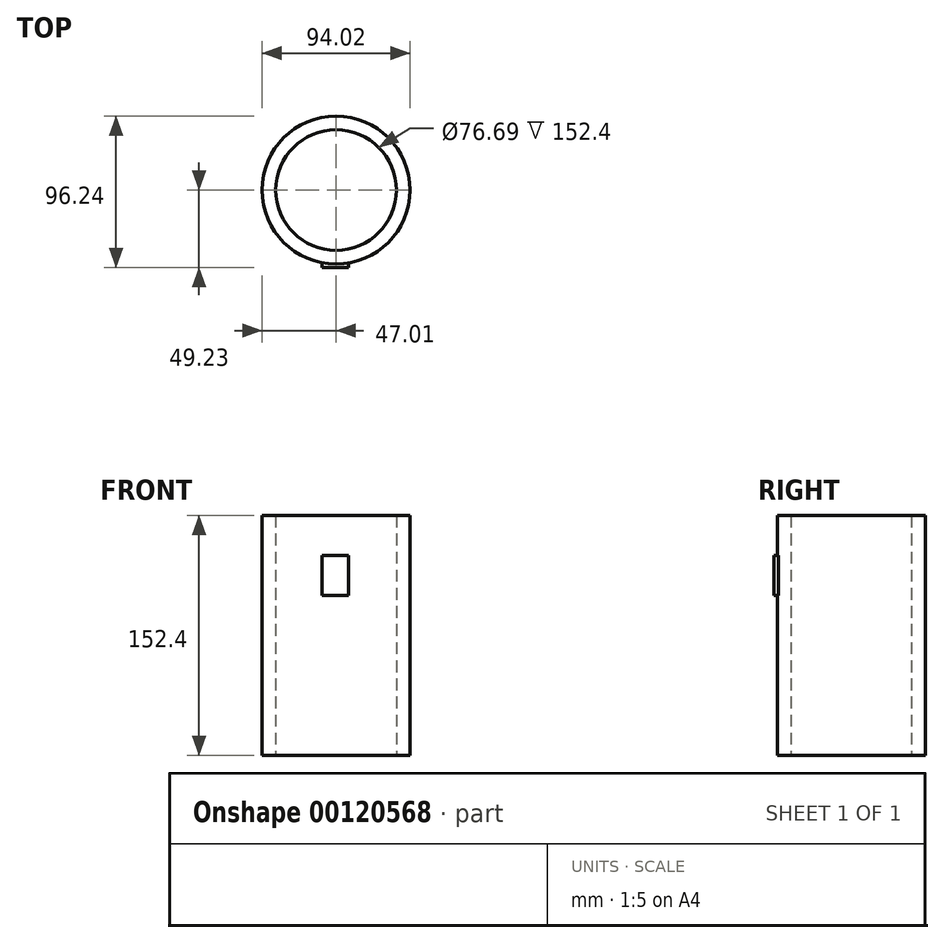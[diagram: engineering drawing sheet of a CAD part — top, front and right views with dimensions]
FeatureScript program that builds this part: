
annotation { "Feature Type Name" : "Feature", "Feature Type Description" : "" }
export const myFeature = defineFeature(function(context is Context, id is Id, definition is map)
    precondition{}
    {
        {
            var Q0;
            Q0=qCreatedBy(makeId("Top.planeOp"),FACE);
            var sketch = newSketch(context, id + "F0", { "sketchPlane" : qUnion([Q0])});
            skCircle(sketch, "E0", {"center": v(0, 0) * mm, "radius": 38.34 * mm});
            skCircle(sketch, "E1", {"center": v(0, 0) * mm, "radius": 47.01 * mm});
            skSolve(sketch);
        }
        {
            var Q0;
            Q0=makeQuery(id+"F0.imprint","IMPRINT",FACE,{"disambiguationData":[TD([[makeQuery(id+"F0.imprint","IMPRINT",EDGE,{"derivedFrom":sQuery(id+"F0.wireOp",EDGE,"E0")}),-1.0]])]});
            extrude(context, id + "F1", {"entities" : qUnion([Q0]), "depth" : 101.6 * mm});
        }
        {
            var Q0;
            Q0=makeQuery(id+"F1.opExtrude","CAP_FACE",FACE,{"disambiguationData":[OSD([sQuery(id+"F0.wireOp",EDGE,"E0"),sQuery(id+"F0.wireOp",EDGE,"E1")])],"isStart":false});
            var sketch = newSketch(context, id + "F2", { "sketchPlane" : qUnion([Q0])});
            skLineSegment(sketch, "E2", {"start": v(-6.36, -46.58) * mm, "end": v(-6.36, -37.81) * mm});
            skSolve(sketch);
        }
        {
            var Q0;
            Q0=makeQuery(id+"F1.opExtrude","CAP_FACE",FACE,{"disambiguationData":[OSD([sQuery(id+"F0.wireOp",EDGE,"E0"),sQuery(id+"F0.wireOp",EDGE,"E1")])],"isStart":false});
            var sketch = newSketch(context, id + "F3", { "sketchPlane" : qUnion([Q0])});
            skLineSegment(sketch, "E3.bottom", {"start": v(-8.8, 50.98) * mm, "end": v(7.93, 50.98) * mm});
            skLineSegment(sketch, "E3.top", {"start": v(-8.8, -49.23) * mm, "end": v(7.93, -49.23) * mm});
            skLineSegment(sketch, "E3.left", {"start": v(-8.8, 50.98) * mm, "end": v(-8.8, -49.23) * mm});
            skLineSegment(sketch, "E3.right", {"start": v(7.93, 50.98) * mm, "end": v(7.93, -49.23) * mm});
            skSolve(sketch);
        }
        {
            var Q0;
            Q0 = qSketchRegion(id + "F2", true);
            var Q1;
            Q1=makeQuery(id+"F1.opExtrude","CAP_FACE",FACE,{"disambiguationData":[OSD([sQuery(id+"F0.wireOp",EDGE,"E0"),sQuery(id+"F0.wireOp",EDGE,"E1")])],"isStart":false});
            extrude(context, id + "F4", {"entities" : qUnion([Q0, Q1]), "operationType" : NewBodyOperationType.ADD, "depth" : 25.4 * mm});
        }
        {
            var Q0;
            Q0=makeQuery(id+"F4.opExtrude","CAP_FACE",FACE,{"disambiguationData":[OSD([sQuery(id+"F0.wireOp",EDGE,"E0"),sQuery(id+"F0.wireOp",EDGE,"E1")])],"isStart":false});
            extrude(context, id + "F5", {"entities" : qUnion([Q0]), "operationType" : NewBodyOperationType.ADD, "depth" : 25.4 * mm});
        }
        {
            var Q0;
            {var subQ0=sQuery(id+"F3.wireOp",EDGE,"E3.top");Q0=makeQuery(id+"F3.imprint","IMPRINT",FACE,{"disambiguationData":[TD([[makeQuery(id+"F3.imprint","IMPRINT",EDGE,{"derivedFrom":subQ0}),1.0]])]});}
            extrude(context, id + "F6", {"entities" : qUnion([Q0]), "operationType" : NewBodyOperationType.ADD, "depth" : 25.4 * mm});
        }
    });
